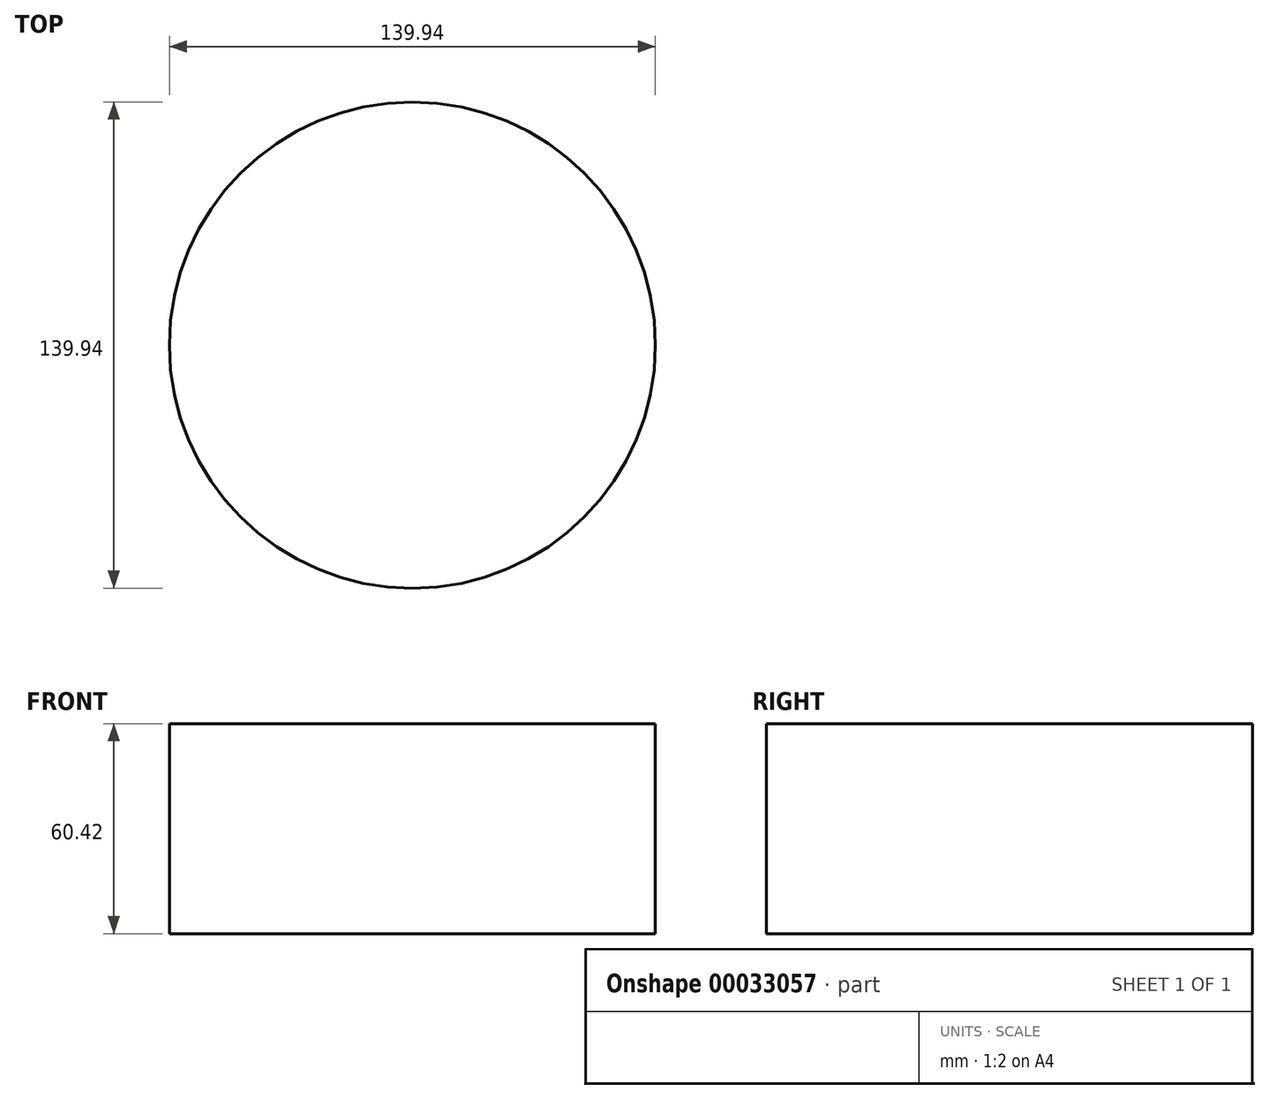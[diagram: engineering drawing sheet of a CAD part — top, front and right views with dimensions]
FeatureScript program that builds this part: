
annotation { "Feature Type Name" : "Feature", "Feature Type Description" : "" }
export const myFeature = defineFeature(function(context is Context, id is Id, definition is map)
    precondition{}
    {
        {
            var Q0;
            Q0=qCreatedBy(makeId("Top.planeOp"),FACE);
            var sketch = newSketch(context, id + "F0", { "sketchPlane" : qUnion([Q0])});
            skCircle(sketch, "E0", {"center": v(0, 0) * mm, "radius": 69.97 * mm});
            skSolve(sketch);
        }
        {
            var Q0;
            Q0=makeQuery(id+"F0.imprint","IMPRINT",FACE,{"disambiguationData":[TD([[makeQuery(id+"F0.imprint","IMPRINT",EDGE,{"derivedFrom":sQuery(id+"F0.wireOp",EDGE,"E0")}),1.0]])]});
            extrude(context, id + "F1", {"entities" : qUnion([Q0]), "depth" : 60.42 * mm});
        }
    });
